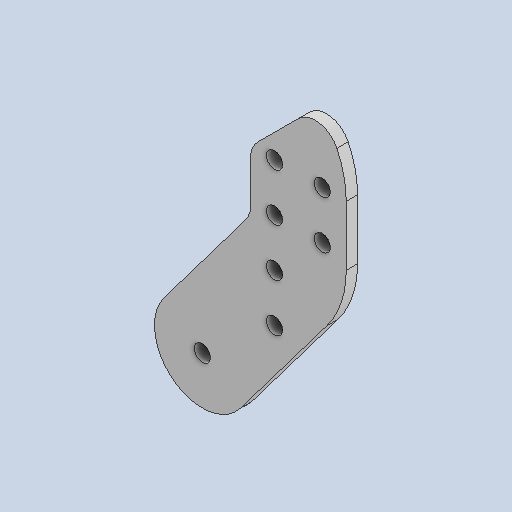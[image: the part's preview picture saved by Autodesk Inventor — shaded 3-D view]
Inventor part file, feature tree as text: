
AUTODESK INVENTOR PART (.ipt)
format: ipt  version: 2023 (Build 270158000, 158)  size: 177,664 bytes
history: native  units: in
note: dims shown in document units (in); Inventor stores cm internally (conversion verified against a paired STEP export)
features: extrude x1, fillet x1, sketch x1
ambient origin geometry x8: Origin, YZ Plane, XZ Plane, XY Plane, X Axis, Y Axis, Z Axis, Center Point
bodies: Solid1 (feature_tree)
feature tree (3):
  extrude  "Extrusion1"  Depth=1.0in
  fillet  "Fillet1"  Radius=1.5in
  sketch  "Sketch1"  dims[d0=0.17in d1=1.0in d2=1.5in d3=0.505in d4=0.625in d5=1.0in d6=45.0deg d7=0.17in d8=0.7874in d10=0.5in d11=0.7874in d13=0.5in d17=0.5in d18=0.5in d19=0.1181in d20=0.0in d21=0.25in]
